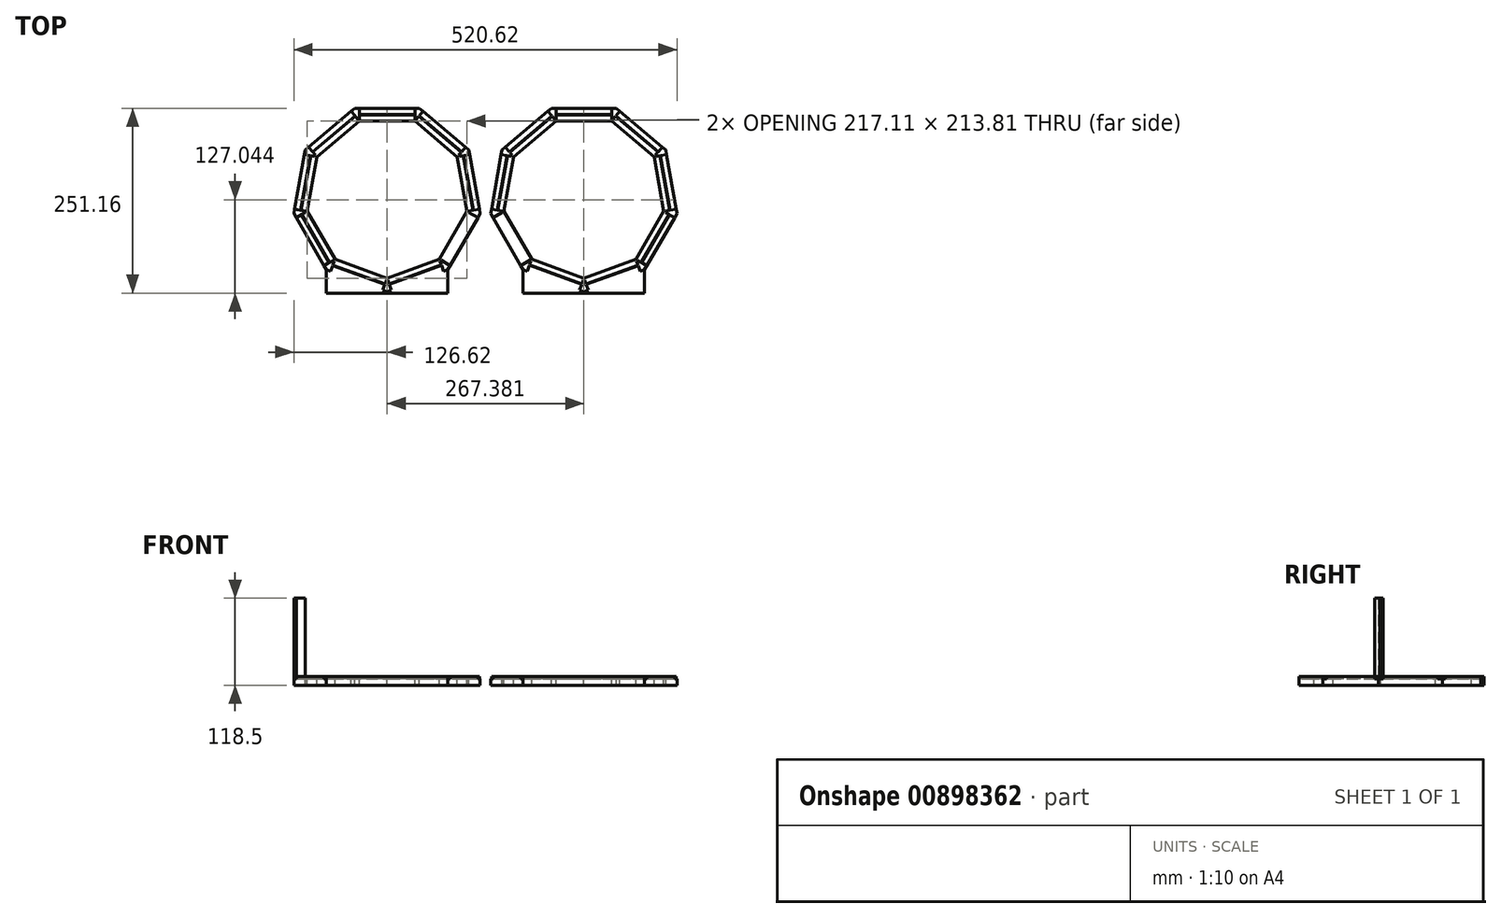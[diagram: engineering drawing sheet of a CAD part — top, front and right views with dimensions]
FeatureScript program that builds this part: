
annotation { "Feature Type Name" : "Feature", "Feature Type Description" : "" }
export const myFeature = defineFeature(function(context is Context, id is Id, definition is map)
    precondition{}
    {
        {
            var Q0;
            Q0=qCreatedBy(makeId("Top.planeOp"),FACE);
            var sketch = newSketch(context, id + "F0", { "sketchPlane" : qUnion([Q0])});
            skLineSegment(sketch, "E0", {"start": v(144.21, -83.72) * mm, "end": v(34.04, -83.72) * mm});
            skLineSegment(sketch, "E1", {"start": v(34.04, -83.72) * mm, "end": v(34.04, -62.46) * mm});
            skLineSegment(sketch, "E2", {"start": v(34.04, -62.46) * mm, "end": v(4.73, -11.69) * mm});
            skLineSegment(sketch, "E3", {"start": v(4.73, -11.69) * mm, "end": v(14.91, 46.04) * mm});
            skLineSegment(sketch, "E4", {"start": v(14.91, 46.04) * mm, "end": v(59.82, 83.72) * mm});
            skLineSegment(sketch, "E5", {"start": v(59.82, 83.72) * mm, "end": v(118.44, 83.72) * mm});
            skLineSegment(sketch, "E6", {"start": v(118.44, 83.72) * mm, "end": v(163.34, 46.04) * mm});
            skLineSegment(sketch, "E7", {"start": v(163.34, 46.04) * mm, "end": v(173.52, -11.69) * mm});
            skLineSegment(sketch, "E8", {"start": v(173.52, -11.69) * mm, "end": v(144.21, -62.46) * mm});
            skLineSegment(sketch, "E9", {"start": v(144.21, -62.46) * mm, "end": v(144.21, -83.72) * mm});
            skLineSegment(sketch, "E10", {"start": v(136.36, -53.1) * mm, "end": v(89.13, -70.3) * mm});
            skLineSegment(sketch, "E11", {"start": v(89.13, -70.3) * mm, "end": v(41.9, -53.1) * mm});
            skLineSegment(sketch, "E12", {"start": v(41.9, -53.1) * mm, "end": v(16.76, -9.57) * mm});
            skLineSegment(sketch, "E13", {"start": v(16.76, -9.57) * mm, "end": v(25.49, 39.93) * mm});
            skLineSegment(sketch, "E14", {"start": v(25.49, 39.93) * mm, "end": v(64, 72.25) * mm});
            skLineSegment(sketch, "E15", {"start": v(64, 72.25) * mm, "end": v(114.26, 72.25) * mm});
            skLineSegment(sketch, "E16", {"start": v(114.26, 72.25) * mm, "end": v(152.77, 39.93) * mm});
            skLineSegment(sketch, "E17", {"start": v(152.77, 39.93) * mm, "end": v(161.5, -9.57) * mm});
            skLineSegment(sketch, "E18", {"start": v(161.5, -9.57) * mm, "end": v(136.36, -53.1) * mm});
            skLineSegment(sketch, "E19", {"start": v(59.8, 83.72) * mm, "end": v(56.6, 81.04) * mm});
            skLineSegment(sketch, "E20", {"start": v(56.6, 81.04) * mm, "end": v(60.16, 76.8) * mm});
            skLineSegment(sketch, "E21", {"start": v(60.16, 76.8) * mm, "end": v(21.66, 44.5) * mm});
            skLineSegment(sketch, "E22", {"start": v(21.66, 44.5) * mm, "end": v(18.1, 48.73) * mm});
            skLineSegment(sketch, "E23", {"start": v(18.1, 48.73) * mm, "end": v(14.9, 46.05) * mm});
            skLineSegment(sketch, "E24", {"start": v(14.9, 46.05) * mm, "end": v(14.18, 41.94) * mm});
            skLineSegment(sketch, "E25", {"start": v(14.18, 41.94) * mm, "end": v(19.6, 40.98) * mm});
            skLineSegment(sketch, "E26", {"start": v(19.6, 40.98) * mm, "end": v(10.87, -8.51) * mm});
            skLineSegment(sketch, "E27", {"start": v(10.87, -8.51) * mm, "end": v(5.46, -7.56) * mm});
            skLineSegment(sketch, "E28", {"start": v(5.46, -7.56) * mm, "end": v(4.73, -11.67) * mm});
            skLineSegment(sketch, "E29", {"start": v(4.73, -11.67) * mm, "end": v(6.82, -15.3) * mm});
            skLineSegment(sketch, "E30", {"start": v(6.82, -15.3) * mm, "end": v(15.11, -10.5) * mm});
            skLineSegment(sketch, "E31", {"start": v(15.11, -10.5) * mm, "end": v(14.89, -9.22) * mm});
            skLineSegment(sketch, "E32", {"start": v(14.89, -9.22) * mm, "end": v(11.31, -8.6) * mm});
            skLineSegment(sketch, "E33", {"start": v(11.31, -8.6) * mm, "end": v(20.04, 40.9) * mm});
            skLineSegment(sketch, "E34", {"start": v(20.04, 40.9) * mm, "end": v(23.61, 40.27) * mm});
            skLineSegment(sketch, "E35", {"start": v(23.61, 40.27) * mm, "end": v(24.26, 41.4) * mm});
            skLineSegment(sketch, "E36", {"start": v(24.26, 41.4) * mm, "end": v(21.95, 44.15) * mm});
            skLineSegment(sketch, "E37", {"start": v(21.95, 44.15) * mm, "end": v(60.44, 76.46) * mm});
            skLineSegment(sketch, "E38", {"start": v(60.44, 76.46) * mm, "end": v(62.76, 73.7) * mm});
            skLineSegment(sketch, "E39", {"start": v(62.76, 73.7) * mm, "end": v(63.98, 74.14) * mm});
            skLineSegment(sketch, "E40", {"start": v(63.98, 74.14) * mm, "end": v(63.98, 77.77) * mm});
            skLineSegment(sketch, "E41", {"start": v(63.98, 77.77) * mm, "end": v(114.27, 77.77) * mm});
            skLineSegment(sketch, "E42", {"start": v(114.27, 77.77) * mm, "end": v(114.27, 74.14) * mm});
            skLineSegment(sketch, "E43", {"start": v(114.27, 74.14) * mm, "end": v(115.49, 73.7) * mm});
            skLineSegment(sketch, "E44", {"start": v(115.49, 73.7) * mm, "end": v(121.64, 81.04) * mm});
            skLineSegment(sketch, "E45", {"start": v(121.64, 81.04) * mm, "end": v(118.45, 83.72) * mm});
            skLineSegment(sketch, "E46", {"start": v(118.45, 83.72) * mm, "end": v(114.27, 83.72) * mm});
            skLineSegment(sketch, "E47", {"start": v(114.27, 83.72) * mm, "end": v(114.27, 78.22) * mm});
            skLineSegment(sketch, "E48", {"start": v(114.27, 78.22) * mm, "end": v(63.98, 78.22) * mm});
            skLineSegment(sketch, "E49", {"start": v(63.98, 78.22) * mm, "end": v(63.98, 83.72) * mm});
            skLineSegment(sketch, "E50", {"start": v(63.98, 83.72) * mm, "end": v(59.8, 83.72) * mm});
            skLineSegment(sketch, "E51", {"start": v(118.15, 76.85) * mm, "end": v(117.86, 76.5) * mm});
            skLineSegment(sketch, "E52", {"start": v(117.86, 76.5) * mm, "end": v(156.35, 44.21) * mm});
            skLineSegment(sketch, "E53", {"start": v(156.35, 44.21) * mm, "end": v(154, 41.4) * mm});
            skLineSegment(sketch, "E54", {"start": v(154, 41.4) * mm, "end": v(154.64, 40.28) * mm});
            skLineSegment(sketch, "E55", {"start": v(154.64, 40.28) * mm, "end": v(158.2, 40.9) * mm});
            skLineSegment(sketch, "E56", {"start": v(158.2, 40.9) * mm, "end": v(166.93, -8.62) * mm});
            skLineSegment(sketch, "E57", {"start": v(166.93, -8.62) * mm, "end": v(163.38, -9.24) * mm});
            skLineSegment(sketch, "E58", {"start": v(163.38, -9.24) * mm, "end": v(163.16, -10.52) * mm});
            skLineSegment(sketch, "E59", {"start": v(163.16, -10.52) * mm, "end": v(166.3, -12.34) * mm});
            skLineSegment(sketch, "E60", {"start": v(166.3, -12.34) * mm, "end": v(141.16, -55.87) * mm});
            skLineSegment(sketch, "E61", {"start": v(141.16, -55.87) * mm, "end": v(138, -54.04) * mm});
            skLineSegment(sketch, "E62", {"start": v(138, -54.04) * mm, "end": v(137.01, -54.88) * mm});
            skLineSegment(sketch, "E63", {"start": v(137.01, -54.88) * mm, "end": v(138.27, -58.34) * mm});
            skLineSegment(sketch, "E64", {"start": v(138.27, -58.34) * mm, "end": v(91.04, -75.53) * mm});
            skLineSegment(sketch, "E65", {"start": v(91.04, -75.53) * mm, "end": v(89.8, -72.13) * mm});
            skLineSegment(sketch, "E66", {"start": v(89.8, -72.13) * mm, "end": v(88.5, -72.13) * mm});
            skLineSegment(sketch, "E67", {"start": v(88.5, -72.13) * mm, "end": v(87.3, -75.47) * mm});
            skLineSegment(sketch, "E68", {"start": v(87.3, -75.47) * mm, "end": v(40, -58.26) * mm});
            skLineSegment(sketch, "E69", {"start": v(40, -58.26) * mm, "end": v(41.23, -54.87) * mm});
            skLineSegment(sketch, "E70", {"start": v(41.23, -54.87) * mm, "end": v(40.24, -54.04) * mm});
            skLineSegment(sketch, "E71", {"start": v(40.24, -54.04) * mm, "end": v(31.94, -58.83) * mm});
            skLineSegment(sketch, "E72", {"start": v(31.94, -58.83) * mm, "end": v(34.03, -62.44) * mm});
            skLineSegment(sketch, "E73", {"start": v(34.03, -62.44) * mm, "end": v(37.96, -63.87) * mm});
            skLineSegment(sketch, "E74", {"start": v(37.96, -63.87) * mm, "end": v(39.85, -58.68) * mm});
            skLineSegment(sketch, "E75", {"start": v(39.85, -58.68) * mm, "end": v(87.14, -75.9) * mm});
            skLineSegment(sketch, "E76", {"start": v(87.14, -75.9) * mm, "end": v(85.23, -81.13) * mm});
            skLineSegment(sketch, "E77", {"start": v(85.23, -81.13) * mm, "end": v(89.16, -82.56) * mm});
            skLineSegment(sketch, "E78", {"start": v(89.16, -82.56) * mm, "end": v(93.08, -81.13) * mm});
            skLineSegment(sketch, "E79", {"start": v(93.08, -81.13) * mm, "end": v(91.2, -75.95) * mm});
            skLineSegment(sketch, "E80", {"start": v(91.2, -75.95) * mm, "end": v(138.43, -58.76) * mm});
            skLineSegment(sketch, "E81", {"start": v(138.43, -58.76) * mm, "end": v(140.3, -63.88) * mm});
            skLineSegment(sketch, "E82", {"start": v(140.3, -63.88) * mm, "end": v(144.22, -62.45) * mm});
            skLineSegment(sketch, "E83", {"start": v(144.22, -62.45) * mm, "end": v(146.3, -58.83) * mm});
            skLineSegment(sketch, "E84", {"start": v(146.3, -58.83) * mm, "end": v(141.55, -56.1) * mm});
            skLineSegment(sketch, "E85", {"start": v(141.55, -56.1) * mm, "end": v(166.69, -12.56) * mm});
            skLineSegment(sketch, "E86", {"start": v(166.69, -12.56) * mm, "end": v(171.45, -15.31) * mm});
            skLineSegment(sketch, "E87", {"start": v(171.45, -15.31) * mm, "end": v(173.54, -11.7) * mm});
            skLineSegment(sketch, "E88", {"start": v(173.54, -11.7) * mm, "end": v(172.82, -7.58) * mm});
            skLineSegment(sketch, "E89", {"start": v(172.82, -7.58) * mm, "end": v(167.37, -8.54) * mm});
            skLineSegment(sketch, "E90", {"start": v(167.37, -8.54) * mm, "end": v(158.64, 40.99) * mm});
            skLineSegment(sketch, "E91", {"start": v(158.64, 40.99) * mm, "end": v(164.07, 41.95) * mm});
            skLineSegment(sketch, "E92", {"start": v(164.07, 41.95) * mm, "end": v(163.35, 46.06) * mm});
            skLineSegment(sketch, "E93", {"start": v(163.35, 46.06) * mm, "end": v(160.15, 48.74) * mm});
            skLineSegment(sketch, "E94", {"start": v(160.15, 48.74) * mm, "end": v(156.64, 44.56) * mm});
            skLineSegment(sketch, "E95", {"start": v(156.64, 44.56) * mm, "end": v(118.15, 76.85) * mm});
            skLineSegment(sketch, "E96", {"start": v(-144.21, -83.72) * mm, "end": v(-34.04, -83.72) * mm});
            skLineSegment(sketch, "E97", {"start": v(-136.36, -53.1) * mm, "end": v(-89.13, -70.3) * mm});
            skLineSegment(sketch, "E98", {"start": v(-89.13, -70.3) * mm, "end": v(-41.9, -53.1) * mm});
            skLineSegment(sketch, "E99", {"start": v(-41.9, -53.1) * mm, "end": v(-16.76, -9.57) * mm});
            skLineSegment(sketch, "E100", {"start": v(-16.76, -9.57) * mm, "end": v(-25.49, 39.93) * mm});
            skLineSegment(sketch, "E101", {"start": v(-25.49, 39.93) * mm, "end": v(-64, 72.25) * mm});
            skLineSegment(sketch, "E102", {"start": v(-64, 72.25) * mm, "end": v(-114.26, 72.25) * mm});
            skLineSegment(sketch, "E103", {"start": v(-114.26, 72.25) * mm, "end": v(-152.77, 39.93) * mm});
            skLineSegment(sketch, "E104", {"start": v(-152.77, 39.93) * mm, "end": v(-161.5, -9.57) * mm});
            skLineSegment(sketch, "E105", {"start": v(-161.5, -9.57) * mm, "end": v(-136.36, -53.1) * mm});
            skLineSegment(sketch, "E106", {"start": v(-118.45, 83.72) * mm, "end": v(-121.64, 81.04) * mm});
            skLineSegment(sketch, "E107", {"start": v(-121.64, 81.04) * mm, "end": v(-121.64, 81.03) * mm});
            skLineSegment(sketch, "E108", {"start": v(-115.49, 73.7) * mm, "end": v(-114.27, 74.14) * mm});
            skLineSegment(sketch, "E109", {"start": v(-114.27, 74.14) * mm, "end": v(-114.27, 77.77) * mm});
            skLineSegment(sketch, "E110", {"start": v(-114.27, 77.77) * mm, "end": v(-63.98, 77.77) * mm});
            skLineSegment(sketch, "E111", {"start": v(-63.98, 77.77) * mm, "end": v(-63.98, 74.14) * mm});
            skLineSegment(sketch, "E112", {"start": v(-63.98, 74.14) * mm, "end": v(-62.76, 73.7) * mm});
            skLineSegment(sketch, "E113", {"start": v(-62.76, 73.7) * mm, "end": v(-60.44, 76.46) * mm});
            skLineSegment(sketch, "E114", {"start": v(-60.44, 76.46) * mm, "end": v(-21.95, 44.15) * mm});
            skLineSegment(sketch, "E115", {"start": v(-21.95, 44.15) * mm, "end": v(-24.26, 41.4) * mm});
            skLineSegment(sketch, "E116", {"start": v(-24.26, 41.4) * mm, "end": v(-23.61, 40.27) * mm});
            skLineSegment(sketch, "E117", {"start": v(-23.61, 40.27) * mm, "end": v(-20.04, 40.9) * mm});
            skLineSegment(sketch, "E118", {"start": v(-20.04, 40.9) * mm, "end": v(-11.31, -8.6) * mm});
            skLineSegment(sketch, "E119", {"start": v(-11.31, -8.6) * mm, "end": v(-14.89, -9.22) * mm});
            skLineSegment(sketch, "E120", {"start": v(-14.89, -9.22) * mm, "end": v(-15.11, -10.5) * mm});
            skLineSegment(sketch, "E121", {"start": v(-15.11, -10.5) * mm, "end": v(-6.82, -15.3) * mm});
            skLineSegment(sketch, "E122", {"start": v(-6.82, -15.3) * mm, "end": v(-4.73, -11.67) * mm});
            skLineSegment(sketch, "E123", {"start": v(-4.73, -11.67) * mm, "end": v(-5.46, -7.56) * mm});
            skLineSegment(sketch, "E124", {"start": v(-5.46, -7.56) * mm, "end": v(-10.87, -8.51) * mm});
            skLineSegment(sketch, "E125", {"start": v(-10.87, -8.51) * mm, "end": v(-19.6, 40.98) * mm});
            skLineSegment(sketch, "E126", {"start": v(-19.6, 40.98) * mm, "end": v(-14.18, 41.94) * mm});
            skLineSegment(sketch, "E127", {"start": v(-14.18, 41.94) * mm, "end": v(-14.9, 46.05) * mm});
            skLineSegment(sketch, "E128", {"start": v(-14.9, 46.05) * mm, "end": v(-18.1, 48.73) * mm});
            skLineSegment(sketch, "E129", {"start": v(-18.1, 48.73) * mm, "end": v(-21.66, 44.5) * mm});
            skLineSegment(sketch, "E130", {"start": v(-21.66, 44.5) * mm, "end": v(-60.16, 76.8) * mm});
            skLineSegment(sketch, "E131", {"start": v(-60.16, 76.8) * mm, "end": v(-56.6, 81.04) * mm});
            skLineSegment(sketch, "E132", {"start": v(-56.6, 81.04) * mm, "end": v(-59.8, 83.72) * mm});
            skLineSegment(sketch, "E133", {"start": v(-59.8, 83.72) * mm, "end": v(-63.98, 83.72) * mm});
            skLineSegment(sketch, "E134", {"start": v(-63.98, 83.72) * mm, "end": v(-63.98, 78.22) * mm});
            skLineSegment(sketch, "E135", {"start": v(-63.98, 78.22) * mm, "end": v(-114.27, 78.22) * mm});
            skLineSegment(sketch, "E136", {"start": v(-114.27, 78.22) * mm, "end": v(-114.27, 83.72) * mm});
            skLineSegment(sketch, "E137", {"start": v(-114.27, 83.72) * mm, "end": v(-118.45, 83.72) * mm});
            skLineSegment(sketch, "E138", {"start": v(-118.15, 76.85) * mm, "end": v(-156.64, 44.56) * mm});
            skLineSegment(sketch, "E139", {"start": v(-156.64, 44.56) * mm, "end": v(-160.15, 48.74) * mm});
            skLineSegment(sketch, "E140", {"start": v(-160.15, 48.74) * mm, "end": v(-163.35, 46.06) * mm});
            skLineSegment(sketch, "E141", {"start": v(-163.35, 46.06) * mm, "end": v(-164.07, 41.95) * mm});
            skLineSegment(sketch, "E142", {"start": v(-164.07, 41.95) * mm, "end": v(-158.64, 40.99) * mm});
            skLineSegment(sketch, "E143", {"start": v(-158.64, 40.99) * mm, "end": v(-167.37, -8.54) * mm});
            skLineSegment(sketch, "E144", {"start": v(-167.37, -8.54) * mm, "end": v(-172.82, -7.58) * mm});
            skLineSegment(sketch, "E145", {"start": v(-172.82, -7.58) * mm, "end": v(-173.54, -11.7) * mm});
            skLineSegment(sketch, "E146", {"start": v(-173.54, -11.7) * mm, "end": v(-171.45, -15.31) * mm});
            skLineSegment(sketch, "E147", {"start": v(-171.45, -15.31) * mm, "end": v(-166.69, -12.56) * mm});
            skLineSegment(sketch, "E148", {"start": v(-166.69, -12.56) * mm, "end": v(-141.55, -56.1) * mm});
            skLineSegment(sketch, "E149", {"start": v(-141.55, -56.1) * mm, "end": v(-146.3, -58.83) * mm});
            skLineSegment(sketch, "E150", {"start": v(-146.3, -58.83) * mm, "end": v(-144.22, -62.45) * mm});
            skLineSegment(sketch, "E151", {"start": v(-144.22, -62.45) * mm, "end": v(-140.3, -63.88) * mm});
            skLineSegment(sketch, "E152", {"start": v(-140.3, -63.88) * mm, "end": v(-138.43, -58.76) * mm});
            skLineSegment(sketch, "E153", {"start": v(-138.43, -58.76) * mm, "end": v(-91.2, -75.95) * mm});
            skLineSegment(sketch, "E154", {"start": v(-91.2, -75.95) * mm, "end": v(-93.08, -81.13) * mm});
            skLineSegment(sketch, "E155", {"start": v(-93.08, -81.13) * mm, "end": v(-89.16, -82.56) * mm});
            skLineSegment(sketch, "E156", {"start": v(-89.16, -82.56) * mm, "end": v(-85.23, -81.13) * mm});
            skLineSegment(sketch, "E157", {"start": v(-85.23, -81.13) * mm, "end": v(-87.14, -75.9) * mm});
            skLineSegment(sketch, "E158", {"start": v(-87.14, -75.9) * mm, "end": v(-39.85, -58.68) * mm});
            skLineSegment(sketch, "E159", {"start": v(-39.85, -58.68) * mm, "end": v(-37.96, -63.87) * mm});
            skLineSegment(sketch, "E160", {"start": v(-37.96, -63.87) * mm, "end": v(-34.03, -62.44) * mm});
            skLineSegment(sketch, "E161", {"start": v(-34.03, -62.44) * mm, "end": v(-31.94, -58.83) * mm});
            skLineSegment(sketch, "E162", {"start": v(-31.94, -58.83) * mm, "end": v(-40.24, -54.04) * mm});
            skLineSegment(sketch, "E163", {"start": v(-40.24, -54.04) * mm, "end": v(-41.23, -54.87) * mm});
            skLineSegment(sketch, "E164", {"start": v(-41.23, -54.87) * mm, "end": v(-40, -58.26) * mm});
            skLineSegment(sketch, "E165", {"start": v(-40, -58.26) * mm, "end": v(-87.3, -75.47) * mm});
            skLineSegment(sketch, "E166", {"start": v(-87.3, -75.47) * mm, "end": v(-88.5, -72.13) * mm});
            skLineSegment(sketch, "E167", {"start": v(-88.5, -72.13) * mm, "end": v(-89.8, -72.13) * mm});
            skLineSegment(sketch, "E168", {"start": v(-89.8, -72.13) * mm, "end": v(-91.04, -75.53) * mm});
            skLineSegment(sketch, "E169", {"start": v(-91.04, -75.53) * mm, "end": v(-138.27, -58.34) * mm});
            skLineSegment(sketch, "E170", {"start": v(-138.27, -58.34) * mm, "end": v(-137.01, -54.88) * mm});
            skLineSegment(sketch, "E171", {"start": v(-137.01, -54.88) * mm, "end": v(-138, -54.04) * mm});
            skLineSegment(sketch, "E172", {"start": v(-138, -54.04) * mm, "end": v(-141.16, -55.87) * mm});
            skLineSegment(sketch, "E173", {"start": v(-141.16, -55.87) * mm, "end": v(-166.3, -12.34) * mm});
            skLineSegment(sketch, "E174", {"start": v(-166.3, -12.34) * mm, "end": v(-163.16, -10.52) * mm});
            skLineSegment(sketch, "E175", {"start": v(-163.16, -10.52) * mm, "end": v(-163.38, -9.24) * mm});
            skLineSegment(sketch, "E176", {"start": v(-163.38, -9.24) * mm, "end": v(-166.93, -8.62) * mm});
            skLineSegment(sketch, "E177", {"start": v(-166.93, -8.62) * mm, "end": v(-158.2, 40.9) * mm});
            skLineSegment(sketch, "E178", {"start": v(-158.2, 40.9) * mm, "end": v(-154.64, 40.28) * mm});
            skLineSegment(sketch, "E179", {"start": v(-154.64, 40.28) * mm, "end": v(-154, 41.4) * mm});
            skLineSegment(sketch, "E180", {"start": v(-154, 41.4) * mm, "end": v(-156.35, 44.21) * mm});
            skLineSegment(sketch, "E181", {"start": v(-156.35, 44.21) * mm, "end": v(-117.86, 76.5) * mm});
            skLineSegment(sketch, "E182", {"start": v(-121.64, 81.03) * mm, "end": v(-118.15, 76.85) * mm});
            skLineSegment(sketch, "E183", {"start": v(-117.86, 76.5) * mm, "end": v(-115.49, 73.7) * mm});
            skLineSegment(sketch, "E184", {"start": v(-31.94, -58.83) * mm, "end": v(-6.82, -15.3) * mm});
            skLineSegment(sketch, "E185", {"start": v(-5.46, -7.56) * mm, "end": v(-14.18, 41.94) * mm});
            skLineSegment(sketch, "E186", {"start": v(-18.1, 48.73) * mm, "end": v(-56.6, 81.04) * mm});
            skLineSegment(sketch, "E187", {"start": v(-63.98, 83.72) * mm, "end": v(-114.27, 83.72) * mm});
            skLineSegment(sketch, "E188", {"start": v(-121.64, 81.03) * mm, "end": v(-160.15, 48.74) * mm});
            skLineSegment(sketch, "E189", {"start": v(-164.07, 41.95) * mm, "end": v(-172.82, -7.58) * mm});
            skLineSegment(sketch, "E190", {"start": v(-171.45, -15.31) * mm, "end": v(-146.3, -58.83) * mm});
            skLineSegment(sketch, "E191", {"start": v(-144.21, -83.72) * mm, "end": v(-144.22, -62.45) * mm});
            skLineSegment(sketch, "E192", {"start": v(-34.03, -62.44) * mm, "end": v(-34.04, -83.72) * mm});
            skSolve(sketch);
        }
        {
            var Q0;
            Q0=makeQuery(id+"F0.imprint","IMPRINT",FACE,{"disambiguationData":[TD([[makeQuery(id+"F0.imprint","IMPRINT",EDGE,{"derivedFrom":sQuery(id+"F0.wireOp",EDGE,"E129")}),-1.0]])]});
            var Q1;
            Q1=makeQuery(id+"F0.imprint","IMPRINT",FACE,{"disambiguationData":[TD([[makeQuery(id+"F0.imprint","IMPRINT",EDGE,{"derivedFrom":sQuery(id+"F0.wireOp",EDGE,"E124")}),-1.0]])]});
            var Q2;
            Q2=makeQuery(id+"F0.imprint","IMPRINT",FACE,{"disambiguationData":[TD([[makeQuery(id+"F0.imprint","IMPRINT",EDGE,{"derivedFrom":sQuery(id+"F0.wireOp",EDGE,"E147")}),-1.0]])]});
            var Q3;
            Q3=makeQuery(id+"F0.imprint","IMPRINT",FACE,{"disambiguationData":[TD([[makeQuery(id+"F0.imprint","IMPRINT",EDGE,{"derivedFrom":sQuery(id+"F0.wireOp",EDGE,"E142")}),-1.0]])]});
            var Q4;
            Q4=makeQuery(id+"F0.imprint","IMPRINT",FACE,{"disambiguationData":[TD([[makeQuery(id+"F0.imprint","IMPRINT",EDGE,{"derivedFrom":sQuery(id+"F0.wireOp",EDGE,"E134")}),-1.0]])]});
            var Q5;
            Q5=makeQuery(id+"F0.imprint","IMPRINT",FACE,{"disambiguationData":[TD([[makeQuery(id+"F0.imprint","IMPRINT",EDGE,{"derivedFrom":sQuery(id+"F0.wireOp",EDGE,"E138")}),-1.0]])]});
            var Q6;
            Q6=makeQuery(id+"F0.imprint","IMPRINT",FACE,{"disambiguationData":[TD([[makeQuery(id+"F0.imprint","IMPRINT",EDGE,{"derivedFrom":sQuery(id+"F0.wireOp",EDGE,"E97")}),-1.0]])]});
            var Q7;
            Q7=makeQuery(id+"F0.imprint","IMPRINT",FACE,{"disambiguationData":[TD([[makeQuery(id+"F0.imprint","IMPRINT",EDGE,{"derivedFrom":sQuery(id+"F0.wireOp",EDGE,"E96")}),1.0]])]});
            var Q8;
            Q8=makeQuery(id+"F0.imprint","IMPRINT",FACE,{"disambiguationData":[TD([[makeQuery(id+"F0.imprint","IMPRINT",EDGE,{"derivedFrom":sQuery(id+"F0.wireOp",EDGE,"E106")}),1.0]])]});
            extrude(context, id + "F1", {"entities" : qUnion([Q0, Q1, Q2, Q3, Q4, Q5, Q6, Q7, Q8]), "oppositeDirection" : true, "depth" : 8 * mm, "offsetDistance" : 25 * mm});
        }
        {
            var Q0;
            Q0=makeQuery(id+"F0.imprint","IMPRINT",FACE,{"disambiguationData":[TD([[makeQuery(id+"F0.imprint","IMPRINT",EDGE,{"derivedFrom":sQuery(id+"F0.wireOp",EDGE,"E106")}),1.0]])]});
            extrude(context, id + "F2", {"entities" : qUnion([Q0]), "operationType" : NewBodyOperationType.REMOVE, "oppositeDirection" : true, "depth" : 2 * mm, "offsetDistance" : 25 * mm});
        }
        {
            var Q0;
            Q0=makeQuery(id+"F2.boolean.opBoolean","COPY",FACE,{"derivedFrom":makeQuery(id+"F2.opExtrude","CAP_FACE",FACE,{"disambiguationData":[OSD([sQuery(id+"F0.wireOp",EDGE,"E106"),sQuery(id+"F0.wireOp",EDGE,"E107"),sQuery(id+"F0.wireOp",EDGE,"E108"),sQuery(id+"F0.wireOp",EDGE,"E109"),sQuery(id+"F0.wireOp",EDGE,"E110"),sQuery(id+"F0.wireOp",EDGE,"E111"),sQuery(id+"F0.wireOp",EDGE,"E112"),sQuery(id+"F0.wireOp",EDGE,"E113"),sQuery(id+"F0.wireOp",EDGE,"E114"),sQuery(id+"F0.wireOp",EDGE,"E115"),sQuery(id+"F0.wireOp",EDGE,"E116"),sQuery(id+"F0.wireOp",EDGE,"E117"),sQuery(id+"F0.wireOp",EDGE,"E118"),sQuery(id+"F0.wireOp",EDGE,"E119"),sQuery(id+"F0.wireOp",EDGE,"E120"),sQuery(id+"F0.wireOp",EDGE,"E121"),sQuery(id+"F0.wireOp",EDGE,"E122"),sQuery(id+"F0.wireOp",EDGE,"E123"),sQuery(id+"F0.wireOp",EDGE,"E124"),sQuery(id+"F0.wireOp",EDGE,"E125"),sQuery(id+"F0.wireOp",EDGE,"E126"),sQuery(id+"F0.wireOp",EDGE,"E127"),sQuery(id+"F0.wireOp",EDGE,"E128"),sQuery(id+"F0.wireOp",EDGE,"E129"),sQuery(id+"F0.wireOp",EDGE,"E130"),sQuery(id+"F0.wireOp",EDGE,"E131"),sQuery(id+"F0.wireOp",EDGE,"E132"),sQuery(id+"F0.wireOp",EDGE,"E133"),sQuery(id+"F0.wireOp",EDGE,"E134"),sQuery(id+"F0.wireOp",EDGE,"E135"),sQuery(id+"F0.wireOp",EDGE,"E136"),sQuery(id+"F0.wireOp",EDGE,"E137"),sQuery(id+"F0.wireOp",EDGE,"E138"),sQuery(id+"F0.wireOp",EDGE,"E139"),sQuery(id+"F0.wireOp",EDGE,"E140"),sQuery(id+"F0.wireOp",EDGE,"E141"),sQuery(id+"F0.wireOp",EDGE,"E142"),sQuery(id+"F0.wireOp",EDGE,"E143"),sQuery(id+"F0.wireOp",EDGE,"E144"),sQuery(id+"F0.wireOp",EDGE,"E145"),sQuery(id+"F0.wireOp",EDGE,"E146"),sQuery(id+"F0.wireOp",EDGE,"E147"),sQuery(id+"F0.wireOp",EDGE,"E148"),sQuery(id+"F0.wireOp",EDGE,"E149"),sQuery(id+"F0.wireOp",EDGE,"E150"),sQuery(id+"F0.wireOp",EDGE,"E151"),sQuery(id+"F0.wireOp",EDGE,"E152"),sQuery(id+"F0.wireOp",EDGE,"E153"),sQuery(id+"F0.wireOp",EDGE,"E154"),sQuery(id+"F0.wireOp",EDGE,"E155"),sQuery(id+"F0.wireOp",EDGE,"E156"),sQuery(id+"F0.wireOp",EDGE,"E157"),sQuery(id+"F0.wireOp",EDGE,"E158"),sQuery(id+"F0.wireOp",EDGE,"E159"),sQuery(id+"F0.wireOp",EDGE,"E160"),sQuery(id+"F0.wireOp",EDGE,"E161"),sQuery(id+"F0.wireOp",EDGE,"E162"),sQuery(id+"F0.wireOp",EDGE,"E163"),sQuery(id+"F0.wireOp",EDGE,"E164"),sQuery(id+"F0.wireOp",EDGE,"E165"),sQuery(id+"F0.wireOp",EDGE,"E166"),sQuery(id+"F0.wireOp",EDGE,"E167"),sQuery(id+"F0.wireOp",EDGE,"E168"),sQuery(id+"F0.wireOp",EDGE,"E169"),sQuery(id+"F0.wireOp",EDGE,"E170"),sQuery(id+"F0.wireOp",EDGE,"E171"),sQuery(id+"F0.wireOp",EDGE,"E172"),sQuery(id+"F0.wireOp",EDGE,"E173"),sQuery(id+"F0.wireOp",EDGE,"E174"),sQuery(id+"F0.wireOp",EDGE,"E175"),sQuery(id+"F0.wireOp",EDGE,"E176"),sQuery(id+"F0.wireOp",EDGE,"E177"),sQuery(id+"F0.wireOp",EDGE,"E178"),sQuery(id+"F0.wireOp",EDGE,"E179"),sQuery(id+"F0.wireOp",EDGE,"E180"),sQuery(id+"F0.wireOp",EDGE,"E181"),sQuery(id+"F0.wireOp",EDGE,"E182"),sQuery(id+"F0.wireOp",EDGE,"E183")])],"isStart":false})});
            var sketch = newSketch(context, id + "F3", { "sketchPlane" : qUnion([Q0])});
            skLineSegment(sketch, "E193.2", {"start": v(93.08, -81.13) * mm, "end": v(91.2, -75.95) * mm});
            skLineSegment(sketch, "E194", {"start": v(-172.82, -7.58) * mm, "end": v(-173.54, -11.7) * mm});
            skLineSegment(sketch, "E195", {"start": v(-173.54, -11.7) * mm, "end": v(-171.45, -15.31) * mm});
            skLineSegment(sketch, "E196", {"start": v(-171.45, -15.31) * mm, "end": v(-163.16, -10.52) * mm});
            skLineSegment(sketch, "E197", {"start": v(-163.16, -10.52) * mm, "end": v(-163.38, -9.24) * mm});
            skLineSegment(sketch, "E198", {"start": v(-172.82, -7.58) * mm, "end": v(-163.38, -9.24) * mm});
            skSolve(sketch);
        }
        {
            var Q0;
            Q0 = qSketchRegion(id + "F3", true);
            extrude(context, id + "F4", {"entities" : qUnion([Q0]), "depth" : 73 * mm, "offsetDistance" : 25 * mm});
        }
        {
            var Q0;
            Q0=makeQuery(id+"F1.opExtrude","SWEPT_BODY",BODY,{"disambiguationData":[OSD([sQuery(id+"F0.wireOp",EDGE,"E96"),sQuery(id+"F0.wireOp",EDGE,"E97"),sQuery(id+"F0.wireOp",EDGE,"E98"),sQuery(id+"F0.wireOp",EDGE,"E99"),sQuery(id+"F0.wireOp",EDGE,"E100"),sQuery(id+"F0.wireOp",EDGE,"E101"),sQuery(id+"F0.wireOp",EDGE,"E102"),sQuery(id+"F0.wireOp",EDGE,"E103"),sQuery(id+"F0.wireOp",EDGE,"E104"),sQuery(id+"F0.wireOp",EDGE,"E105"),sQuery(id+"F0.wireOp",EDGE,"E106"),sQuery(id+"F0.wireOp",EDGE,"E107"),sQuery(id+"F0.wireOp",EDGE,"E122"),sQuery(id+"F0.wireOp",EDGE,"E123"),sQuery(id+"F0.wireOp",EDGE,"E127"),sQuery(id+"F0.wireOp",EDGE,"E128"),sQuery(id+"F0.wireOp",EDGE,"E132"),sQuery(id+"F0.wireOp",EDGE,"E133"),sQuery(id+"F0.wireOp",EDGE,"E137"),sQuery(id+"F0.wireOp",EDGE,"E140"),sQuery(id+"F0.wireOp",EDGE,"E141"),sQuery(id+"F0.wireOp",EDGE,"E145"),sQuery(id+"F0.wireOp",EDGE,"E146"),sQuery(id+"F0.wireOp",EDGE,"E150"),sQuery(id+"F0.wireOp",EDGE,"E161"),sQuery(id+"F0.wireOp",EDGE,"E184"),sQuery(id+"F0.wireOp",EDGE,"E185"),sQuery(id+"F0.wireOp",EDGE,"E186"),sQuery(id+"F0.wireOp",EDGE,"E187"),sQuery(id+"F0.wireOp",EDGE,"E188"),sQuery(id+"F0.wireOp",EDGE,"E189"),sQuery(id+"F0.wireOp",EDGE,"E190"),sQuery(id+"F0.wireOp",EDGE,"E191"),sQuery(id+"F0.wireOp",EDGE,"E192")])]});
            var Q1;
            Q1=makeQuery(id+"F6.opPattern","COPY",BODY,{"derivedFrom":makeQuery(id+"F1.opExtrude","SWEPT_BODY",BODY,{"disambiguationData":[OSD([sQuery(id+"F0.wireOp",EDGE,"E96"),sQuery(id+"F0.wireOp",EDGE,"E97"),sQuery(id+"F0.wireOp",EDGE,"E98"),sQuery(id+"F0.wireOp",EDGE,"E99"),sQuery(id+"F0.wireOp",EDGE,"E100"),sQuery(id+"F0.wireOp",EDGE,"E101"),sQuery(id+"F0.wireOp",EDGE,"E102"),sQuery(id+"F0.wireOp",EDGE,"E103"),sQuery(id+"F0.wireOp",EDGE,"E104"),sQuery(id+"F0.wireOp",EDGE,"E105"),sQuery(id+"F0.wireOp",EDGE,"E106"),sQuery(id+"F0.wireOp",EDGE,"E107"),sQuery(id+"F0.wireOp",EDGE,"E122"),sQuery(id+"F0.wireOp",EDGE,"E123"),sQuery(id+"F0.wireOp",EDGE,"E127"),sQuery(id+"F0.wireOp",EDGE,"E128"),sQuery(id+"F0.wireOp",EDGE,"E132"),sQuery(id+"F0.wireOp",EDGE,"E133"),sQuery(id+"F0.wireOp",EDGE,"E137"),sQuery(id+"F0.wireOp",EDGE,"E140"),sQuery(id+"F0.wireOp",EDGE,"E141"),sQuery(id+"F0.wireOp",EDGE,"E145"),sQuery(id+"F0.wireOp",EDGE,"E146"),sQuery(id+"F0.wireOp",EDGE,"E150"),sQuery(id+"F0.wireOp",EDGE,"E161"),sQuery(id+"F0.wireOp",EDGE,"E184"),sQuery(id+"F0.wireOp",EDGE,"E185"),sQuery(id+"F0.wireOp",EDGE,"E186"),sQuery(id+"F0.wireOp",EDGE,"E187"),sQuery(id+"F0.wireOp",EDGE,"E188"),sQuery(id+"F0.wireOp",EDGE,"E189"),sQuery(id+"F0.wireOp",EDGE,"E190"),sQuery(id+"F0.wireOp",EDGE,"E191"),sQuery(id+"F0.wireOp",EDGE,"E192")])]}),"instanceName":"1"});
            var Q2;
            Q2=makeQuery(id+"F4.opExtrude","SWEPT_BODY",BODY,{"disambiguationData":[OSD([sQuery(id+"F3.wireOp",EDGE,"E194"),sQuery(id+"F3.wireOp",EDGE,"E195"),sQuery(id+"F3.wireOp",EDGE,"E196"),sQuery(id+"F3.wireOp",EDGE,"E197"),sQuery(id+"F3.wireOp",EDGE,"E198")])]});
            var Q3;
            Q3=qCreatedBy(makeId("Origin.pointOp"),VERTEX);
            transform(context, id + "F5", {"entities" : qUnion([Q0, Q1, Q2]), "transformType" : TransformType.SCALE_UNIFORMLY, "scale" : 1.5, "scalePoint" : qUnion([Q3]), "makeCopy" : false});
        }
        {
            var Q0;
            Q0=makeQuery(id+"F1.opExtrude","SWEPT_BODY",BODY,{"disambiguationData":[OSD([sQuery(id+"F0.wireOp",EDGE,"E96"),sQuery(id+"F0.wireOp",EDGE,"E97"),sQuery(id+"F0.wireOp",EDGE,"E98"),sQuery(id+"F0.wireOp",EDGE,"E99"),sQuery(id+"F0.wireOp",EDGE,"E100"),sQuery(id+"F0.wireOp",EDGE,"E101"),sQuery(id+"F0.wireOp",EDGE,"E102"),sQuery(id+"F0.wireOp",EDGE,"E103"),sQuery(id+"F0.wireOp",EDGE,"E104"),sQuery(id+"F0.wireOp",EDGE,"E105"),sQuery(id+"F0.wireOp",EDGE,"E106"),sQuery(id+"F0.wireOp",EDGE,"E107"),sQuery(id+"F0.wireOp",EDGE,"E122"),sQuery(id+"F0.wireOp",EDGE,"E123"),sQuery(id+"F0.wireOp",EDGE,"E127"),sQuery(id+"F0.wireOp",EDGE,"E128"),sQuery(id+"F0.wireOp",EDGE,"E132"),sQuery(id+"F0.wireOp",EDGE,"E133"),sQuery(id+"F0.wireOp",EDGE,"E137"),sQuery(id+"F0.wireOp",EDGE,"E140"),sQuery(id+"F0.wireOp",EDGE,"E141"),sQuery(id+"F0.wireOp",EDGE,"E145"),sQuery(id+"F0.wireOp",EDGE,"E146"),sQuery(id+"F0.wireOp",EDGE,"E150"),sQuery(id+"F0.wireOp",EDGE,"E161"),sQuery(id+"F0.wireOp",EDGE,"E184"),sQuery(id+"F0.wireOp",EDGE,"E185"),sQuery(id+"F0.wireOp",EDGE,"E186"),sQuery(id+"F0.wireOp",EDGE,"E187"),sQuery(id+"F0.wireOp",EDGE,"E188"),sQuery(id+"F0.wireOp",EDGE,"E189"),sQuery(id+"F0.wireOp",EDGE,"E190"),sQuery(id+"F0.wireOp",EDGE,"E191"),sQuery(id+"F0.wireOp",EDGE,"E192")])]});
            var Q1;
            Q1=qCreatedBy(makeId("Right.planeOp"),FACE);
            mirror(context, id + "F6", {"entities" : qUnion([Q0]), "mirrorPlane" : qUnion([Q1])});
        }
    });
